# Revit family: ГРЕЕРС ВС-1320С
name_source: partatom
category: Оборудование
units: mm (PartAtom-declared; Revit-internal decimal feet)

## family parameters
Общий = Нет
Основа = Грань
При загрузке вырезать с полостями = Нет
Размер круглого соединителя = Использовать диаметр
Тип детали = Нормальный
Точка расчета площади = Нет

## types (1)
- ГРЕЕРС ВС-1320С
    URL = https://greers.ru
    Вентилятор = Осевой, однофазный, переменного тока, с 3-х скоростным двигателем
    Изготовитель = ООО "ЮНИО-ВЕНТ"
    Класс защиты = IP54
    Классификация нагрузок = Двигатель
    Количество воды проходящей через теплообменник = 0.0 л/с
    Коэффициент мощности = 1
    Максимальное потребление тока = 0 А
    Напряжение питания = 230 В
    Описание = ГРЕЕРС ВС-1320С
    Отметка по умолчанию = 2500 мм
    Падение давления воды в теплообменнике = 0.0 Па
    Патрубки = 15 мм
    Полная установленная мощность = 0 В·А
    Производительность = 0.0 м³/ч
    Стоимость = 21295 $
    Температура воды на входе в теплообменник = 0 °C
    Температура воды на выходе из теплообменника = 0 °C
    Температура воздуха на входе в аппарат = 0 °C
    Температура воздуха на выходе из аппарата = 0 °C
    Тепловая мощность = 0 Вт
    Частота = 50 Гц
